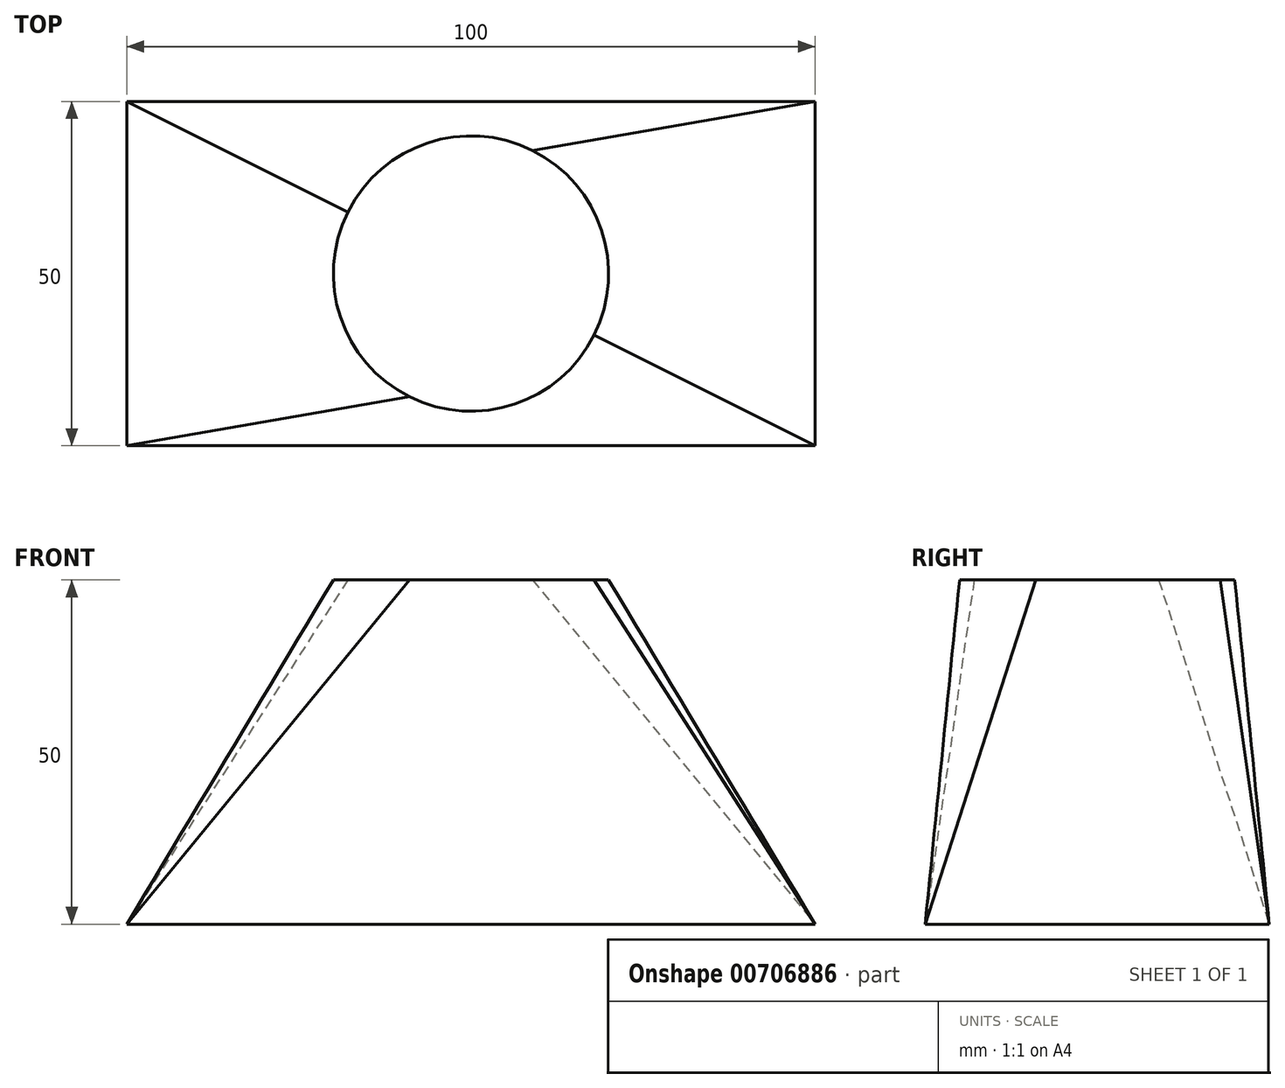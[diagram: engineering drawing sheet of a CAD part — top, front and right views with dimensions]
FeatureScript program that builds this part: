
annotation { "Feature Type Name" : "Feature", "Feature Type Description" : "" }
export const myFeature = defineFeature(function(context is Context, id is Id, definition is map)
    precondition{}
    {
        {
            var Q0;
            Q0=qCreatedBy(makeId("Top.planeOp"),FACE);
            var sketch = newSketch(context, id + "F0", { "sketchPlane" : qUnion([Q0])});
            skLineSegment(sketch, "E0.bottom", {"start": v(-50, 0) * mm, "end": v(50, 0) * mm});
            skLineSegment(sketch, "E0.top", {"start": v(-50, -50) * mm, "end": v(50, -50) * mm});
            skLineSegment(sketch, "E0.left", {"start": v(-50, 0) * mm, "end": v(-50, -50) * mm});
            skLineSegment(sketch, "E0.right", {"start": v(50, 0) * mm, "end": v(50, -50) * mm});
            skSolve(sketch);
        }
        {
            var Q0;
            Q0=qCreatedBy(makeId("Top.planeOp"),FACE);
            cPlane(context, id + "F1", {"entities" : qUnion([Q0]), "cplaneType" : CPlaneType.OFFSET, "offset" : 50 * mm, "width" : 150 * mm, "height" : 150 * mm});
        }
        {
            var Q0;
            Q0=qCreatedBy(id+"F1.planeOp",FACE);
            var sketch = newSketch(context, id + "F2", { "sketchPlane" : qUnion([Q0])});
            skCircle(sketch, "E1", {"center": v(0, -25) * mm, "radius": 20 * mm});
            skSolve(sketch);
        }
        {
            var Q0;
            Q0=makeQuery(id+"F2.imprint","IMPRINT",FACE,{"disambiguationData":[TD([[makeQuery(id+"F2.imprint","IMPRINT",EDGE,{"derivedFrom":sQuery(id+"F2.wireOp",EDGE,"E1")}),1.0]])]});
            var Q1;
            Q1=makeQuery(id+"F0.imprint","IMPRINT",FACE,{"disambiguationData":[TD([[makeQuery(id+"F0.imprint","IMPRINT",EDGE,{"derivedFrom":sQuery(id+"F0.wireOp",EDGE,"E0.bottom")}),-1.0]])]});
            loft(context, id + "F3", {"sheetProfilesArray" : [{ "sheetProfileEntities" : qUnion([Q0]) }, { "sheetProfileEntities" : qUnion([Q1]) }]});
        }
    });
